# Revit family: 63_UN_LF_SM_Titan SQ7_LI
name_source: partatom
category: Lighting Fixtures
units: mm (PartAtom-declared; Revit-internal decimal feet)

## family parameters
Always vertical = Yes
Cut with Voids When Loaded = Yes
Light Source = No
OmniClass Number = 23.80.70.11.14
OmniClass Title = General Luminaries, Directional
Part Type = Normal
Room Calculation Point = Yes
Round Connector Dimension = Use Diameter
Shared = No
Work Plane-Based = No

## types (2) — shared parameters
Assembly Code = 63.0
Housing_Material = Plastic, Opaque Black
IfcExportAs = IfcLightFixtureType
IfcExportType = USERDEFINED
Lamp = LED
Manufacturer = Light International
Model = Titan SQ
Type Comments = SQ7
URL = https://lightinternational.nl
Voltage = 230 V

## per-type parameters (varying)
| type | Apparent Load | Lightsource_tilt | Luminous Flux (lm) | Wattage Comments |
| SQ7 - Wall mounted | 10 VA | 90.00° | 2000 lm | 10W |
| SQ7 - Ceiling mounted | 6 VA | 180.00° | 994 lm | 6.2W |

## geometry (parser evidence)
native form markers: Sweep x15
no freeform markers — native parametric forms only
